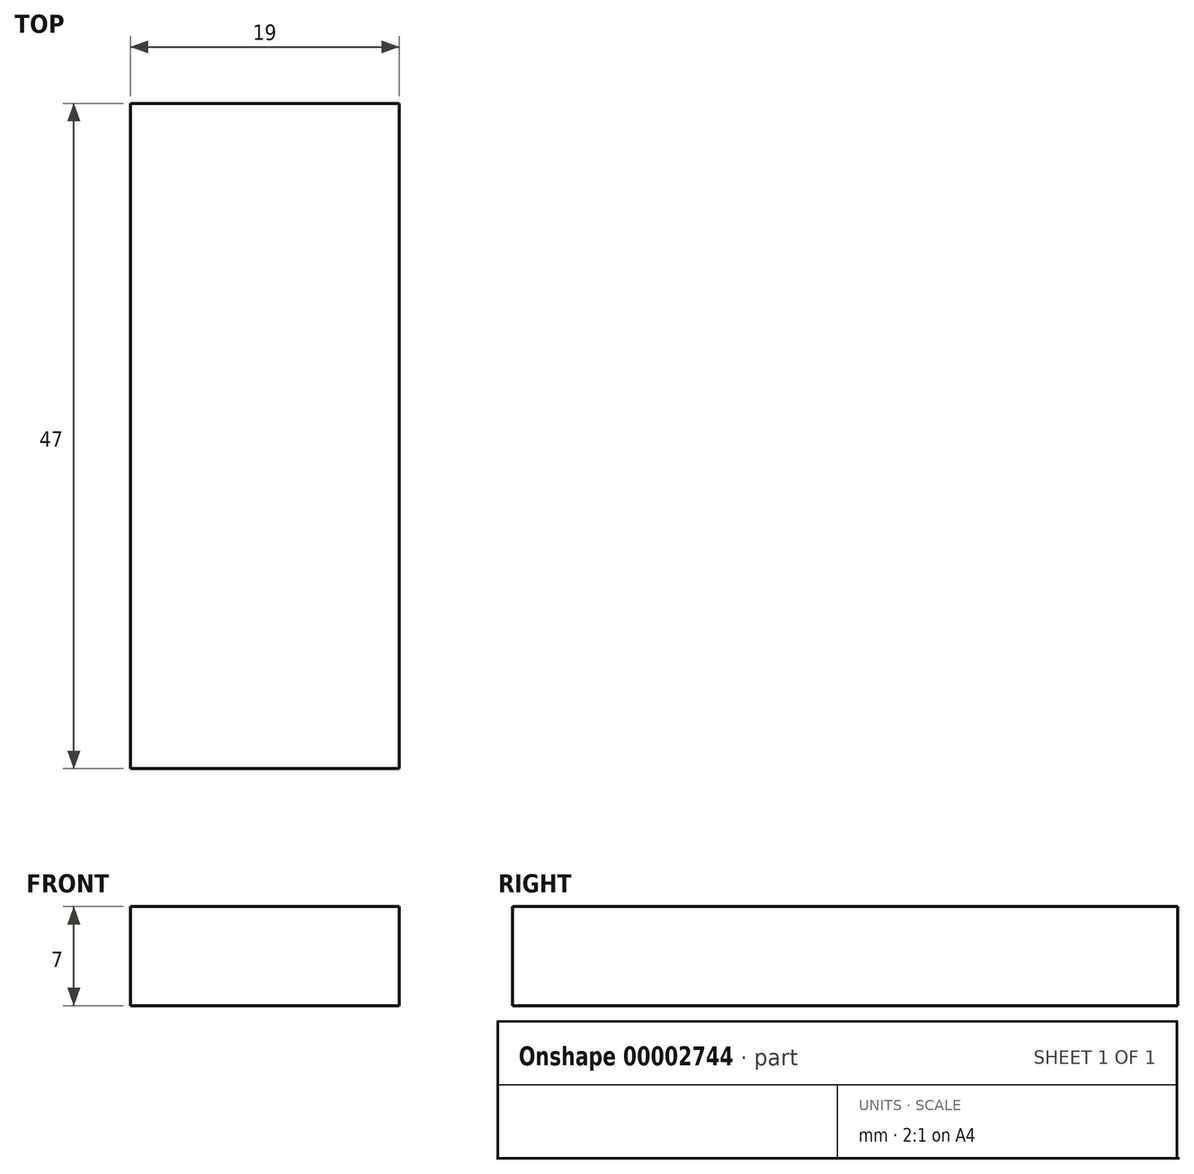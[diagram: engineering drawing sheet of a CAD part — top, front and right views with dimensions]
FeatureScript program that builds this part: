
annotation { "Feature Type Name" : "Feature", "Feature Type Description" : "" }
export const myFeature = defineFeature(function(context is Context, id is Id, definition is map)
    precondition{}
    {
        {
            var Q0;
            Q0=qCreatedBy(makeId("Top.planeOp"),FACE);
            var sketch = newSketch(context, id + "F0", { "sketchPlane" : qUnion([Q0])});
            skLineSegment(sketch, "E0.bottom", {"start": v(9.5, 23.5) * mm, "end": v(-9.5, 23.5) * mm});
            skLineSegment(sketch, "E0.top", {"start": v(9.5, -23.5) * mm, "end": v(-9.5, -23.5) * mm});
            skLineSegment(sketch, "E0.left", {"start": v(9.5, 23.5) * mm, "end": v(9.5, -23.5) * mm});
            skLineSegment(sketch, "E0.right", {"start": v(-9.5, 23.5) * mm, "end": v(-9.5, -23.5) * mm});
            skPoint(sketch, "E0.middle", {"position": v(0, 0) * mm});
            skSolve(sketch);
        }
        {
            var Q0;
            Q0 = qSketchRegion(id + "F0", true);
            extrude(context, id + "F1", {"entities" : qUnion([Q0]), "depth" : 7 * mm});
        }
    });
